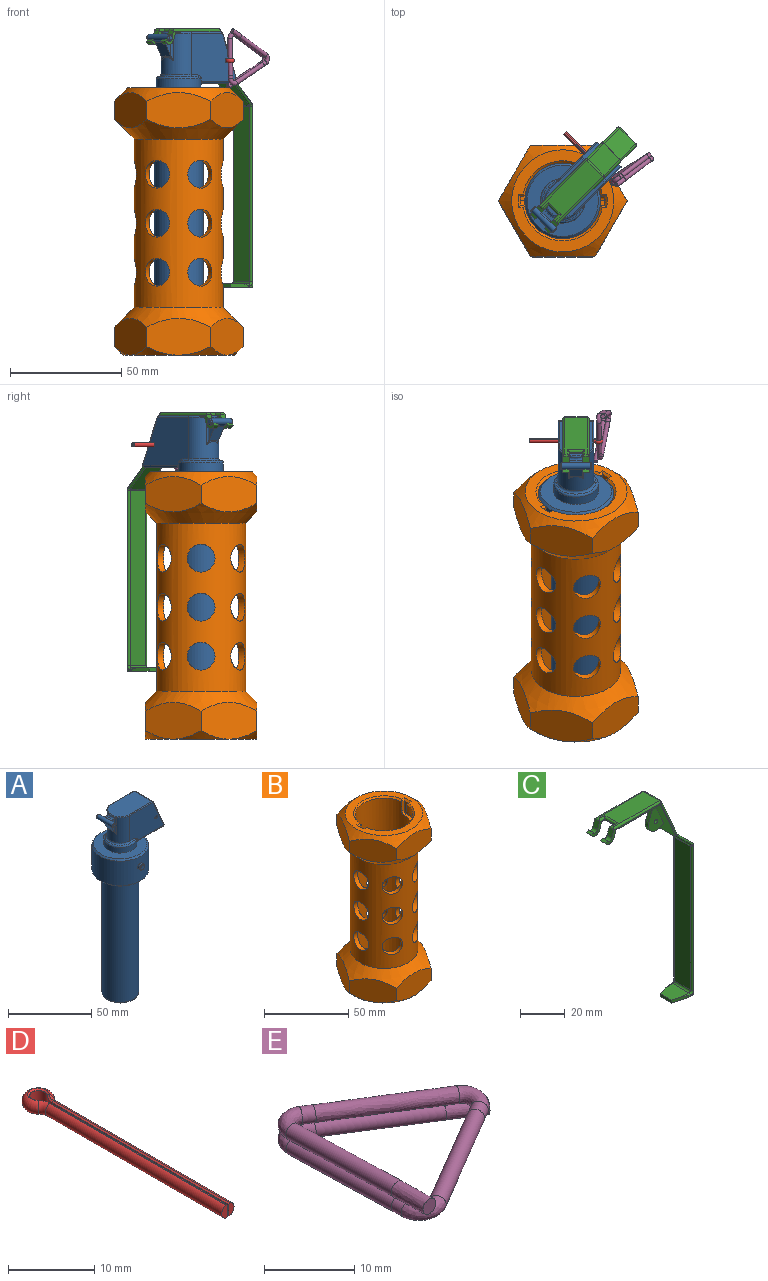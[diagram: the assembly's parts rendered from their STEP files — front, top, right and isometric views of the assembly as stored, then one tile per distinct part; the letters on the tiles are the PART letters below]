
ASSEMBLY  parts=5 mates=4
PART A: 67 faces, bbox 46.6x38x135.1 mm
  f0: plane 21x15mm, normal (0.92,0,0.4), area 313.5mm2, adj f26,f43,f49,f50,f60,f62,f63,f64
  f1: cylinder r=17mm len=34mm, axis (0,0,1), area 1897.4mm2, adj f6,f7,f10,f11
  f2: cylinder r=11mm len=89mm, axis (0,0,1), area 6151.2mm2, adj f4,f44
  f3: plane 20x20mm, normal (0,0,-1), area 314.2mm2, adj f44
  f4: plane 32x32mm, normal (0,0,-1), area 424.1mm2, adj f2,f10
  f5: plane 32x32mm, normal (0,0,1), area 490.1mm2, adj f11,f12
  f6: cylinder r=2mm len=4mm, axis (0,1,0), area 18.8mm2, adj f1,f58
  f7: cylinder r=2mm len=4mm, axis (0,1,0), area 18.8mm2, adj f1,f59
  f8: cylinder r=19mm len=3.08mm, axis (0,0,-1), area 7.3mm2, adj f59
  f9: cylinder r=19mm len=3.08mm, axis (0,0,-1), area 7.3mm2, adj f58
  f10: cone r=17mm half-angle=45deg, axis (0,0,1), area 146.6mm2, adj f1,f4
  f11: cone r=16mm half-angle=45deg, axis (0,0,-1), area 146.6mm2, adj f1,f5
  f12: cylinder r=10mm len=20mm, axis (0,0,-1), area 196.3mm2, adj f5,f27,f28,f30,f31,f33,f34
  f13: plane 28.98x21.5mm, normal (0,1,0), area 503mm2, adj f15,f29,f33,f35,f47,f49,f51,f53
  f14: plane 28.98x21.5mm, normal (0,-1,0), area 503mm2, adj f15,f25,f30,f32,f48,f50,f52,f54
  f15: cylinder r=8mm len=18.5mm, axis (0,0,-1), area 384mm2, adj f13,f14,f36,f37,f38,f39,f40,f55
  f16: plane 26.84x15mm, normal (0,0,1), area 378.5mm2, adj f43,f53,f54,f55
  f17: plane 19.99x14mm, normal (0,0,-1), area 255.8mm2, adj f25,f26,f28,f29
  f18: plane 9.37x4.31mm, normal (0,-1,0), area 19.5mm2, adj f20,f21,f22,f38,f40,f41,f42
  f19: plane 9.37x4.31mm, normal (0,1,0), area 19.5mm2, adj f20,f21,f22,f37,f38,f41,f42
  f20: plane 6x1.73mm, normal (0,0,1), area 8.3mm2, adj f18,f19,f38,f41
  f21: plane 7.28x6.28mm, normal (-0.87,0,-0.5), area 45.6mm2, adj f18,f19,f37,f39,f40,f42
  f22: cylinder r=1.5mm len=13mm, axis (0,1,0), area 99.1mm2, adj f18,f19,f41,f42,f56,f57
  f23: plane 2x2mm, normal (0,-1,0), area 3.1mm2, adj f57
  f24: plane 2x2mm, normal (0,1,0), area 3.1mm2, adj f56
  f25: cylinder r=1mm len=22.65mm, axis (1,0,0), area 33.5mm2, adj f14,f17,f27,f46
  f26: cylinder r=1mm len=15mm, axis (0,-1,0), area 28.9mm2, adj f0,f17,f45,f46,f47,f48
  f27: bspline ~2.85x2.21mm, area 3.2mm2, adj f12,f25,f28,f30
  f28: torus R=11mm, axis (0,0,1), area 22.5mm2, adj f12,f17,f27,f31
  f29: cylinder r=1mm len=22.65mm, axis (-1,0,0), area 33.5mm2, adj f13,f17,f31,f45
  f30: cylinder r=1mm len=1mm, axis (0,0,-1), area 0.6mm2, adj f12,f14,f27,f32
  f31: bspline ~2.86x2.31mm, area 3.2mm2, adj f12,f28,f29,f33
  f32: bspline ~7.66x2.25mm, area 7.9mm2, adj f14,f30,f34,f36
  f33: cylinder r=1mm len=1mm, axis (0,0,-1), area 0.6mm2, adj f12,f13,f31,f35
  f34: torus R=9mm, axis (0,0,1), area 57mm2, adj f12,f32,f35,f36
  f35: bspline ~6.84x2.06mm, area 7.9mm2, adj f13,f33,f34,f36
  f36: torus R=9mm, axis (0,0,1), area 41.3mm2, adj f15,f32,f34,f35
  f37: cylinder r=1mm len=12.07mm, axis (0,0,-1), area 11.7mm2, adj f15,f19,f21,f38,f39
  f38: torus R=9mm, axis (0,0,-1), area 10.3mm2, adj f15,f18,f19,f20,f37,f40
  f39: bspline ~8x2.12mm, area 4.3mm2, adj f15,f21,f37,f40
  f40: cylinder r=1mm len=12.07mm, axis (0,0,-1), area 11.7mm2, adj f15,f18,f21,f38,f39
  f41: cylinder r=1mm len=6mm, axis (0,1,0), area 4.8mm2, adj f18,f19,f20,f22
  f42: cylinder r=1mm len=6mm, axis (0,1,0), area 4.8mm2, adj f18,f19,f21,f22
  f43: cylinder r=1mm len=15mm, axis (0,-1,0), area 17.4mm2, adj f0,f16,f51,f52
  f44: torus R=10mm, axis (0,0,1), area 105mm2, adj f2,f3
  f45: bspline ~1.19x1mm, area 0.5mm2, adj f26,f29,f47
  f46: bspline ~1.19x1mm, area 0.5mm2, adj f25,f26,f48
  f47: torus R=0.5mm, axis (0,1,0), area 0.3mm2, adj f13,f26,f45,f49
  f48: torus R=0.5mm, axis (0,1,0), area 0.3mm2, adj f14,f26,f46,f50
  f49: cylinder r=0.5mm len=21.2mm, axis (-0.4,0,0.92), area 18mm2, adj f0,f13,f47,f51
  f50: cylinder r=0.5mm len=21.2mm, axis (-0.4,0,0.92), area 18mm2, adj f0,f14,f48,f52
  f51: torus R=0.5mm, axis (0,1,0), area 0.7mm2, adj f13,f43,f49,f53
  f52: torus R=0.5mm, axis (0,1,0), area 0.7mm2, adj f14,f43,f50,f54
  f53: cylinder r=0.5mm len=19.34mm, axis (1,0,0), area 15.2mm2, adj f13,f16,f51,f55
  f54: cylinder r=0.5mm len=19.34mm, axis (-1,0,0), area 15.2mm2, adj f14,f16,f52,f55
  f55: torus R=7.5mm, axis (0,0,1), area 19.3mm2, adj f15,f16,f53,f54
  f56: torus R=1mm, axis (0,-1,0), area 6.5mm2, adj f22,f24
  f57: torus R=1mm, axis (0,-1,0), area 6.5mm2, adj f22,f23
  f58: bspline ~4.01x4mm, area 8.8mm2, adj f6,f9
  f59: bspline ~4.01x4mm, area 8.8mm2, adj f7,f8
  f60: plane 8.51x3.35mm, normal (0.93,0,-0.37), area 18.3mm2, adj f0,f61,f63,f64
  f61: cylinder r=5mm len=6.99mm, axis (0,-1,0), area 23.6mm2, adj f60,f62,f63,f64
  f62: plane 2.69x2mm, normal (-0.4,0,0.92), area 5.9mm2, adj f0,f61,f63,f64
  f63: plane 15.34x9.68mm, normal (0,-1,0), area 78.5mm2, adj f0,f60,f61,f62,f66
  f64: plane 15.34x9.68mm, normal (0,1,0), area 78.5mm2, adj f0,f60,f61,f62,f65
  f65: cylinder r=1mm len=7mm, axis (0,-1,0), area 44mm2, adj f14,f64
  f66: cylinder r=1mm len=7mm, axis (0,-1,0), area 44mm2, adj f13,f63
PART B: 71 faces, bbox 57.8x57.8x120 mm
  f0: cylinder r=17mm len=113mm, axis (0,0,1), area 9648.4mm2, adj f1,f2,f28,f29,f30,f31,f32,f33
  f1: plane 4.5x2.01mm, normal (0,1,0), area 9.1mm2, adj f0,f48,f61,f64
  f2: plane 4.5x2.01mm, normal (0,-1,0), area 9.1mm2, adj f0,f50,f62,f69
  f3: plane 45.8x45.8mm, normal (0,0,1), area 605.5mm2, adj f19,f63,f64,f65,f66,f67,f68,f69
  f4: plane 28.88x15.91mm, normal (0,1,0), area 382.4mm2, adj f5,f9,f18,f19
  f5: plane 25x15.92mm, normal (-0.87,0.5,0), area 382.4mm2, adj f4,f6,f18,f19
  f6: plane 25x15.92mm, normal (-0.87,-0.5,0), area 382.4mm2, adj f5,f7,f18,f19
  f7: plane 28.88x15.91mm, normal (0,-1,0), area 382.4mm2, adj f6,f8,f18,f19
  f8: plane 25x15.92mm, normal (0.87,-0.5,0), area 382.4mm2, adj f7,f9,f18,f19
  f9: plane 25x15.92mm, normal (0.87,0.5,0), area 382.4mm2, adj f4,f8,f18,f19
  f10: cylinder r=20mm len=75.5mm, axis (0,0,-1), area 7250.1mm2, adj f17,f18,f29,f30,f31,f32,f33,f34
  f11: plane 28.9x16.52mm, normal (0,1,0), area 399.7mm2, adj f12,f16,f17,f21,f25
  f12: plane 25x16.52mm, normal (-0.87,0.5,0), area 399.7mm2, adj f11,f13,f17,f24,f25
  f13: plane 25x16.52mm, normal (-0.87,-0.5,0), area 399.7mm2, adj f12,f14,f17,f23,f24
  f14: plane 28.9x16.52mm, normal (0,-1,0), area 399.7mm2, adj f13,f15,f17,f22,f23
  f15: plane 25x16.51mm, normal (0.87,-0.5,0), area 399.7mm2, adj f14,f16,f17,f20,f22
  f16: plane 25x16.52mm, normal (0.87,0.5,0), area 399.7mm2, adj f11,f15,f17,f20,f21
  f17: cone r=20mm half-angle=45deg, axis (0,0,-1), area 1284.7mm2, adj f10,f11,f12,f13,f14,f15,f16
  f18: cone r=31mm half-angle=45deg, axis (0,0,1), area 1284.7mm2, adj f4,f5,f6,f7,f8,f9,f10
  f19: cone r=28.9mm half-angle=45deg, axis (0,0,-1), area 732mm2, adj f3,f4,f5,f6,f7,f8,f9
  f20: cone r=28.9mm half-angle=45deg, axis (0,0,1), area 47.5mm2, adj f15,f16,f26
  f21: cone r=28.9mm half-angle=45deg, axis (0,0,1), area 47.5mm2, adj f11,f16,f26
  f22: cone r=28.9mm half-angle=45deg, axis (0,0,1), area 47.5mm2, adj f14,f15,f26
  f23: cone r=28.9mm half-angle=45deg, axis (0,0,1), area 47.5mm2, adj f13,f14,f26
  f24: cone r=28.9mm half-angle=45deg, axis (0,0,1), area 47.5mm2, adj f12,f13,f26
  f25: cone r=28.9mm half-angle=45deg, axis (0,0,1), area 47.5mm2, adj f11,f12,f26
  f26: plane 50x50mm, normal (0,0,-1), area 1950.9mm2, adj f20,f21,f22,f23,f24,f25,f27
  f27: cone r=2mm half-angle=45deg, axis (0,0,-1), area 17.8mm2, adj f26
  f28: plane 34x34mm, normal (0,0,1), area 907.9mm2, adj f0
  f29: cylinder r=6.25mm len=12.92mm, axis (-0.5,0.87,0), area 121.5mm2, adj f0,f10
  f30: cylinder r=6.25mm len=12.92mm, axis (-0.5,0.87,0), area 121.4mm2, adj f0,f10
  f31: cylinder r=6.25mm len=12.92mm, axis (-0.5,0.87,0), area 121.5mm2, adj f0,f10
  f32: cylinder r=6.25mm len=12.92mm, axis (-0.5,0.87,0), area 121.4mm2, adj f0,f10
  f33: cylinder r=6.25mm len=12.92mm, axis (-0.5,0.87,0), area 121.5mm2, adj f0,f10
  f34: cylinder r=6.25mm len=12.92mm, axis (-0.5,0.87,0), area 121.4mm2, adj f0,f10
  f35: cylinder r=6.25mm len=12.92mm, axis (-0.5,-0.87,0), area 121.5mm2, adj f0,f10
  f36: cylinder r=6.25mm len=12.92mm, axis (-0.5,-0.87,0), area 121.4mm2, adj f0,f10
  f37: cylinder r=6.25mm len=12.92mm, axis (-0.5,-0.87,0), area 121.5mm2, adj f0,f10
  f38: cylinder r=6.25mm len=12.92mm, axis (-0.5,-0.87,0), area 121.4mm2, adj f0,f10
  f39: cylinder r=6.25mm len=12.92mm, axis (-0.5,-0.87,0), area 121.5mm2, adj f0,f10
  f40: cylinder r=6.25mm len=12.92mm, axis (-0.5,-0.87,0), area 121.4mm2, adj f0,f10
  f41: cylinder r=6.25mm len=12.5mm, axis (-1,0,0), area 121.4mm2, adj f0,f10
  f42: cylinder r=6.25mm len=12.5mm, axis (-1,0,0), area 121.4mm2, adj f0,f10
  f43: cylinder r=6.25mm len=12.5mm, axis (-1,0,0), area 121.4mm2, adj f0,f10
  f44: cylinder r=6.25mm len=12.5mm, axis (-1,0,0), area 121.4mm2, adj f0,f10
  f45: cylinder r=6.25mm len=12.5mm, axis (-1,0,0), area 121.4mm2, adj f0,f10
  f46: cylinder r=6.25mm len=12.5mm, axis (-1,0,0), area 121.4mm2, adj f0,f10
  f47: plane 7x2.01mm, normal (0,-1,0), area 14.1mm2, adj f0,f48,f59,f68
  f48: cylinder r=19mm len=9mm, axis (0,0,1), area 35.2mm2, adj f1,f47,f49,f57,f59,f61,f66
  f49: plane 13.04x7.99mm, normal (0,0,1), area 26.8mm2, adj f0,f48,f56,f57,f59
  f50: cylinder r=19mm len=9mm, axis (0,0,1), area 35.2mm2, adj f2,f51,f52,f58,f60,f62,f67
  f51: plane 7x2.01mm, normal (0,1,0), area 14.1mm2, adj f0,f50,f60,f65
  f52: plane 13.04x7.99mm, normal (0,0,1), area 26.8mm2, adj f0,f50,f55,f58,f60
  f53: plane 10.54x7.83mm, normal (0,0,-1), area 21.8mm2, adj f0,f55,f58,f62
  f54: plane 10.54x7.83mm, normal (0,0,-1), area 21.8mm2, adj f0,f56,f57,f61
  f55: plane 4x2.03mm, normal (-0.04,-1,0), area 8.1mm2, adj f0,f52,f53,f58
  f56: plane 4x2.03mm, normal (0.04,1,0), area 8.1mm2, adj f0,f49,f54,f57
  f57: cylinder r=16.75mm len=11.03mm, axis (0,0,1), area 51.3mm2, adj f48,f49,f54,f56,f61
  f58: cylinder r=16.75mm len=11.03mm, axis (0,0,1), area 51.3mm2, adj f50,f52,f53,f55,f62
  f59: cylinder r=2mm len=2.12mm, axis (-1,0,0), area 6.3mm2, adj f0,f47,f48,f49
  f60: cylinder r=2mm len=2.12mm, axis (1,0,0), area 6.3mm2, adj f0,f50,f51,f52
  f61: cylinder r=0.5mm len=2.08mm, axis (-1,0,0), area 1.6mm2, adj f0,f1,f48,f54,f57
  f62: cylinder r=0.5mm len=2.08mm, axis (1,0,0), area 1.6mm2, adj f0,f2,f50,f53,f58
  f63: cone r=17mm half-angle=45deg, axis (0,0,1), area 70.7mm2, adj f0,f3,f64,f65
  f64: plane 2.91x1.02mm, normal (0,0.71,0.71), area 2.9mm2, adj f1,f3,f63,f66
  f65: plane 2.91x1.02mm, normal (0,0.71,0.71), area 2.9mm2, adj f3,f51,f63,f67
  f66: cone r=19mm half-angle=45deg, axis (0,0,1), area 7.1mm2, adj f3,f48,f64,f68
  f67: cone r=19mm half-angle=45deg, axis (0,0,1), area 7.1mm2, adj f3,f50,f65,f69
  f68: plane 2.91x1.02mm, normal (0,-0.71,0.71), area 2.9mm2, adj f3,f47,f66,f70
  f69: plane 2.91x1.02mm, normal (0,-0.71,0.71), area 2.9mm2, adj f2,f3,f67,f70
  f70: cone r=17mm half-angle=45deg, axis (0,0,1), area 70.7mm2, adj f0,f3,f68,f69
PART C: 73 faces, bbox 56.5x12x116.4 mm
  f0: plane 2.5x1.18mm, normal (0,1,0), area 1.6mm2, adj f18,f28,f55,f56,f57
  f1: plane 2.5x1.18mm, normal (0,-1,0), area 1.6mm2, adj f18,f29,f63,f64,f65
  f2: plane 3.79x3mm, normal (-0.95,0,0.32), area 12mm2, adj f3,f24,f25,f30,f32,f34
  f3: cylinder r=1.5mm len=3mm, axis (0,1,0), area 10.3mm2, adj f2,f4,f24,f25
  f4: plane 3x1.3mm, normal (-0.5,0,0.87), area 4.5mm2, adj f3,f5,f24,f25
  f5: cylinder r=3mm len=5.44mm, axis (0,1,0), area 20.7mm2, adj f4,f6,f24,f25
  f6: plane 3.45x3mm, normal (0.95,0,-0.32), area 10.9mm2, adj f5,f12,f24,f25
  f7: plane 3.79x3mm, normal (-0.95,0,0.32), area 12mm2, adj f8,f23,f26,f33,f35,f37
  f8: cylinder r=1.5mm len=3mm, axis (0,1,0), area 10.3mm2, adj f7,f9,f23,f26
  f9: plane 3x1.3mm, normal (-0.5,0,0.87), area 4.5mm2, adj f8,f10,f23,f26
  f10: cylinder r=3mm len=5.44mm, axis (0,1,0), area 20.7mm2, adj f9,f11,f23,f26
  f11: plane 3.45x3mm, normal (0.95,0,-0.32), area 10.9mm2, adj f10,f12,f23,f26
  f12: plane 27.34x12mm, normal (0,0,-1), area 316.1mm2, adj f6,f11,f23,f24,f25,f26,f27,f66
  f13: plane 22.22x12mm, normal (-0.92,0,-0.4), area 259.9mm2, adj f23,f24,f44,f45,f52,f66,f67,f69
  f14: plane 10x9.57mm, normal (-0.71,0,-0.71), area 135.4mm2, adj f44,f45,f51,f52
  f15: plane 78.59x10mm, normal (-1,0,0), area 785.9mm2, adj f50,f51,f61,f62
  f16: plane 10x9.5mm, normal (0,0,1), area 87.8mm2, adj f17,f28,f29,f55,f61,f65
  f17: plane 7.13x1.5mm, normal (-1,0,0), area 10.7mm2, adj f16,f18,f28,f29
  f18: plane 12x11mm, normal (0,0,-1), area 111.3mm2, adj f0,f1,f17,f28,f29,f60
  f19: plane 80.71x10mm, normal (1,0,0), area 807.1mm2, adj f54,f56,f60,f63
  f20: plane 10x9.81mm, normal (0.71,0,0.71), area 138.7mm2, adj f42,f43,f53,f54
  f21: plane 22.87x10mm, normal (0.92,0,0.4), area 249.3mm2, adj f38,f40,f42,f46
  f22: plane 28.69x10mm, normal (0,0,1), area 260mm2, adj f30,f31,f32,f33,f34,f35,f37,f38
  f23: plane 44.48x21.96mm, normal (0,-1,0), area 39.3mm2, adj f7,f8,f9,f10,f11,f12,f13,f37
  f24: plane 44.48x21.96mm, normal (0,1,0), area 39.3mm2, adj f2,f3,f4,f5,f6,f12,f13,f34
  f25: plane 8.6x6mm, normal (0,-1,0), area 14.6mm2, adj f2,f3,f4,f5,f6,f12,f27,f30
  f26: plane 8.6x6mm, normal (0,1,0), area 14.6mm2, adj f7,f8,f9,f10,f11,f12,f27,f33
  f27: plane 6x0.5mm, normal (-1,0,0), area 3mm2, adj f12,f25,f26,f31
  f28: plane 8.5x2.44mm, normal (-0.28,0.96,0), area 12.5mm2, adj f0,f16,f17,f18,f55
  f29: plane 8.5x2.44mm, normal (-0.28,-0.96,0), area 12.5mm2, adj f1,f16,f17,f18,f65
  f30: cylinder r=1mm len=4.41mm, axis (1,0,0), area 5.3mm2, adj f2,f22,f25,f31,f32
  f31: cylinder r=1mm len=8mm, axis (0,-1,0), area 10.6mm2, adj f22,f27,f30,f33
  f32: cylinder r=1mm len=2.9mm, axis (0,-1,0), area 2.6mm2, adj f2,f22,f30,f34
  f33: cylinder r=1mm len=4.41mm, axis (-1,0,0), area 5.3mm2, adj f7,f22,f26,f31,f35
  f34: cylinder r=1mm len=29.74mm, axis (-1,0,0), area 46.1mm2, adj f2,f22,f24,f32,f36
  f35: cylinder r=1mm len=2.9mm, axis (0,-1,0), area 2.6mm2, adj f7,f22,f33,f37
  f36: sphere r=1mm, area 1.2mm2, adj f34,f38,f40
  f37: cylinder r=1mm len=29.74mm, axis (1,0,0), area 46.1mm2, adj f7,f22,f23,f35,f41
  f38: cylinder r=1mm len=10mm, axis (0,1,0), area 11.6mm2, adj f21,f22,f36,f41
  f39: torus R=2mm, axis (0,-1,0), area 0.6mm2, adj f40,f42,f43,f44
  f40: cylinder r=1mm len=23.26mm, axis (-0.4,0,0.92), area 39.1mm2, adj f21,f24,f36,f39,f44
  f41: sphere r=1mm, area 1.2mm2, adj f37,f38,f46
  f42: cylinder r=1mm len=10mm, axis (0,-1,0), area 3.8mm2, adj f20,f21,f39,f47
  f43: cylinder r=1mm len=10.38mm, axis (-0.71,0,0.71), area 18.3mm2, adj f20,f39,f44,f48,f49
  f44: cylinder r=1mm len=12.21mm, axis (0.71,0,-0.71), area 19.4mm2, adj f13,f14,f24,f39,f40,f43,f45,f49
  f45: cylinder r=1mm len=10.73mm, axis (0,1,0), area 3.9mm2, adj f13,f14,f44,f52
  f46: cylinder r=1mm len=23.26mm, axis (0.4,0,-0.92), area 39.1mm2, adj f21,f23,f41,f47,f52
  f47: torus R=2mm, axis (0,-1,0), area 0.6mm2, adj f42,f46,f52,f53
  f48: sphere r=1mm, area 0.8mm2, adj f43,f49,f54,f56
  f49: torus R=2mm, axis (0,-1,0), area 1.4mm2, adj f43,f44,f48,f50,f51,f56
  f50: cylinder r=1mm len=78.59mm, axis (0,0,-1), area 103.6mm2, adj f15,f49,f56,f57
  f51: cylinder r=1mm len=10mm, axis (0,-1,0), area 7.9mm2, adj f14,f15,f49,f58
  f52: cylinder r=1mm len=12.21mm, axis (-0.71,0,0.71), area 19.4mm2, adj f13,f14,f23,f45,f46,f47,f53,f58
  f53: cylinder r=1mm len=10.38mm, axis (0.71,0,-0.71), area 18.3mm2, adj f20,f47,f52,f58,f59
  f54: cylinder r=1mm len=10mm, axis (0,-1,0), area 7.9mm2, adj f19,f20,f48,f59
  f55: cylinder r=1mm len=4.49mm, axis (-1,0,0), area 3.6mm2, adj f0,f16,f28,f57
  f56: cylinder r=1mm len=81.71mm, axis (0,0,1), area 107.6mm2, adj f0,f19,f48,f49,f50,f57,f60
  f57: torus R=2mm, axis (0,-1,0), area 3.1mm2, adj f0,f50,f55,f56,f61
  f58: torus R=2mm, axis (0,-1,0), area 1.4mm2, adj f51,f52,f53,f59,f62,f63
  f59: sphere r=1mm, area 0.8mm2, adj f53,f54,f58,f63
  f60: cylinder r=1mm len=12mm, axis (0,1,0), area 17.7mm2, adj f18,f19,f56,f63
  f61: cylinder r=1mm len=10mm, axis (0,-1,0), area 15.7mm2, adj f15,f16,f57,f64
  f62: cylinder r=1mm len=78.59mm, axis (0,0,1), area 103.6mm2, adj f15,f58,f63,f64
  f63: cylinder r=1mm len=81.71mm, axis (0,0,-1), area 107.6mm2, adj f1,f19,f58,f59,f60,f62,f64
  f64: torus R=2mm, axis (0,-1,0), area 3.1mm2, adj f1,f61,f62,f63,f65
  f65: cylinder r=1mm len=4.49mm, axis (1,0,0), area 3.6mm2, adj f1,f16,f29,f64
  f66: cylinder r=1mm len=12mm, axis (0,-1,0), area 13.9mm2, adj f12,f13,f23,f24
  f67: plane 8.51x3.35mm, normal (-0.93,0,0.37), area 18.3mm2, adj f13,f68,f71,f72
  f68: cylinder r=5mm len=6.99mm, axis (0,1,0), area 23.6mm2, adj f67,f69,f71,f72
  f69: plane 2.69x2mm, normal (0.4,0,-0.92), area 5.9mm2, adj f13,f68,f71,f72
  f70: cylinder r=1mm len=2mm, axis (0,1,0), area 12.6mm2, adj f71,f72
  f71: plane 15.34x9.68mm, normal (0,-1,0), area 78.5mm2, adj f13,f67,f68,f69,f70
  f72: plane 15.34x9.68mm, normal (0,1,0), area 78.5mm2, adj f13,f67,f68,f69,f70
PART D: 22 faces, bbox 3.8x32.9x2 mm
  f0: plane 1.88x0.9mm, normal (0,-1,0), area 1.3mm2, adj f2,f3,f16,f21
  f1: plane 1.88x0.9mm, normal (0,-1,0), area 1.3mm2, adj f10,f11,f12,f17
  f2: plane 28.85x1.54mm, normal (1,0,0), area 44.4mm2, adj f0,f4,f16,f21
  f3: cylinder r=1mm len=28.85mm, axis (0,1,0), area 70.4mm2, adj f0,f5,f16,f21
  f4: cylinder r=2mm len=1.54mm, axis (0,0,1), area 2.5mm2, adj f2,f6,f15,f20
  f5: torus R=2.1mm, axis (0,0,1), area 2.6mm2, adj f3,f7,f15,f20
  f6: cylinder r=1mm len=2.01mm, axis (0,0,-1), area 7.3mm2, adj f4,f8,f14,f19
  f7: torus R=0.9mm, axis (0,0,-1), area 19.4mm2, adj f5,f9,f14,f19
  f8: cylinder r=2mm len=1.54mm, axis (0,0,1), area 2.5mm2, adj f6,f10,f13,f18
  f9: torus R=2.1mm, axis (0,0,1), area 2.6mm2, adj f7,f11,f13,f18
  f10: plane 28.85x1.54mm, normal (-1,0,0), area 44.4mm2, adj f1,f8,f12,f17
  f11: cylinder r=1mm len=28.85mm, axis (0,-1,0), area 70.4mm2, adj f1,f9,f12,f17
  f12: plane 28.85x0.24mm, normal (-0.57,0,-0.82), area 8.6mm2, adj f1,f10,f11,f13
  f13: cone r=2mm half-angle=55deg, axis (0,0,1), area 0.4mm2, adj f8,f9,f12,f14
  f14: cone r=1mm half-angle=55deg, axis (0,0,-1), area 1.6mm2, adj f6,f7,f13,f15
  f15: cone r=2mm half-angle=55deg, axis (0,0,1), area 0.4mm2, adj f4,f5,f14,f16
  f16: plane 28.85x0.24mm, normal (0.57,0,-0.82), area 8.6mm2, adj f0,f2,f3,f15
  f17: plane 28.85x0.24mm, normal (-0.57,0,0.82), area 8.6mm2, adj f1,f10,f11,f18
  f18: cone r=1.76mm half-angle=55deg, axis (0,0,-1), area 0.4mm2, adj f8,f9,f17,f19
  f19: cone r=1.25mm half-angle=55deg, axis (0,0,1), area 1.6mm2, adj f6,f7,f18,f20
  f20: cone r=1.76mm half-angle=55deg, axis (0,0,-1), area 0.4mm2, adj f4,f5,f19,f21
  f21: plane 28.85x0.24mm, normal (0.57,0,0.82), area 8.6mm2, adj f0,f2,f3,f20
PART E: 17 faces, bbox 25.1x24.8x5.6 mm
  f0: bspline ~5.01x4mm, area 31.4mm2, adj f1,f3,f5,f12
  f1: bspline ~2.03x1.98mm, area 9.7mm2, adj f0,f2,f5,f12
  f2: bspline ~16.55x2.43mm, area 103.6mm2, adj f1,f5,f6,f13
  f3: plane 2.28x2.28mm, normal (0,-1,0), area 3.1mm2, adj f0
  f4: plane 2.28x2.02mm, normal (0.87,-0.49,0), area 3.1mm2, adj f16
  f5: bspline ~16.54x4mm, area 103.9mm2, adj f0,f1,f2,f6
  f6: bspline ~4.47x2.99mm, area 26.1mm2, adj f2,f5,f7,f13
  f7: bspline ~2.49x2.32mm, area 9.7mm2, adj f6,f8,f13,f14
  f8: bspline ~15.3x9.98mm, area 103.7mm2, adj f7,f9,f14,f15,f16
  f9: bspline ~7.12x5.32mm, area 26.3mm2, adj f8,f10,f16
  f10: bspline ~2.48x2.34mm, area 9.8mm2, adj f9,f11
  f11: bspline ~15.32x9.97mm, area 104.1mm2, adj f10,f12
  f12: bspline ~4.49x3mm, area 26.3mm2, adj f0,f1,f11
  f13: bspline ~4.47x3mm, area 26mm2, adj f2,f6,f7,f14
  f14: bspline ~2.5x2.32mm, area 9.7mm2, adj f7,f8,f13,f15
  f15: bspline ~13.95x9.22mm, area 94.1mm2, adj f8,f14,f16
  f16: bspline ~5.31x4.22mm, area 31.5mm2, adj f4,f8,f9,f15
PLACE A rot(axis=(0,0,1),45deg) t=(0,0,120)mm
PLACE B at identity fixed
PLACE C rot(axis=(0,0,1),45deg) t=(-8.49,-8.49,142.5)mm
PLACE D rot(axis=(-0.92,-0.38,0),180deg) t=(1.11,30.56,132.16)mm
PLACE E rot(axis=(0.18,0.81,-0.56),117.3deg) t=(24.14,7.08,145.62)mm
MATE cylindrical A.f1 <-> B.f0  axis (0,0,1) through (0,0,101)mm
MATE revolute C.f3 <-> A.f22  axis (-0.71,0.71,0) through (-5.3,-11.67,142.5)mm
MATE slider D.f11 <-> A.f61  axis (-0.71,0.71,0) through (11.31,20.36,132.16)mm
MATE revolute E.f11 <-> D.f6  axis (0,0,-1) through (23.03,8.64,142.16)mm
